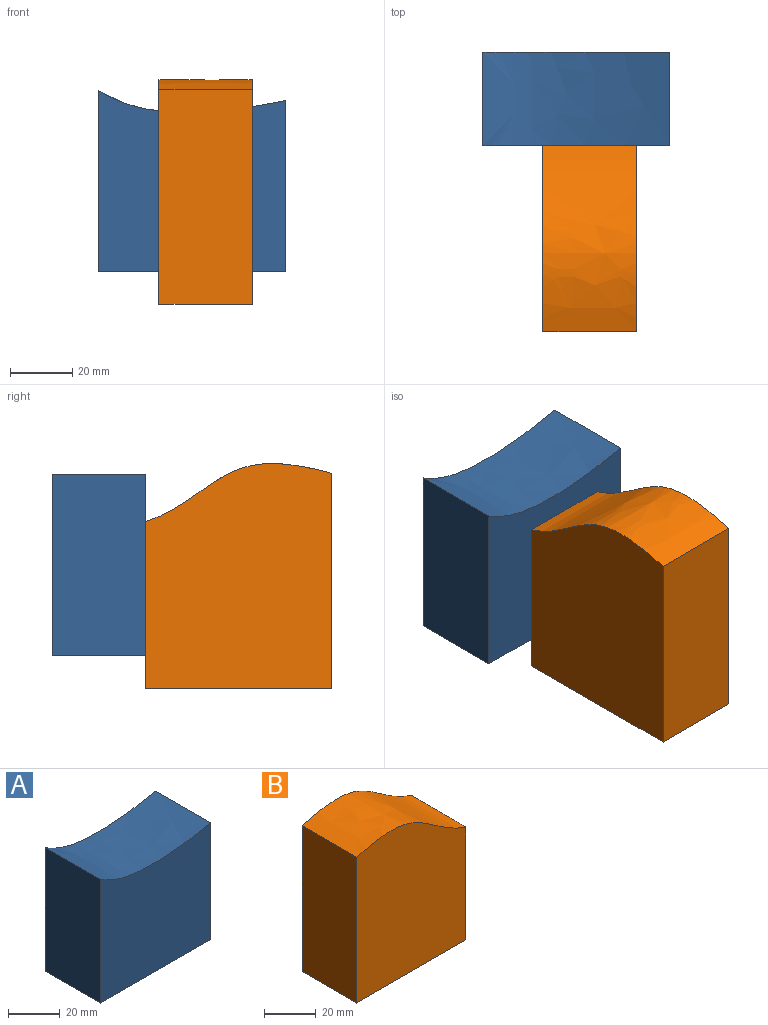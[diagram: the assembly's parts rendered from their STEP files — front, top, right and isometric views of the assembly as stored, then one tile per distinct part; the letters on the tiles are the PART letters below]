
ASSEMBLY  parts=2 mates=1
PART A: 6 faces, bbox 61.7x30x59.2 mm
  f0: extruded ~60x30mm, area 1847.2mm2, adj f2,f3,f4,f5
  f1: plane 60x30mm, normal (0,0,-1), area 1800mm2, adj f2,f3,f4,f5
  f2: plane 61.72x59.16mm, normal (0,1,0), area 3176.1mm2, adj f0,f1,f3,f5
  f3: plane 58.3x30mm, normal (-1,0,0), area 1749.1mm2, adj f0,f1,f2,f4
  f4: plane 61.72x59.16mm, normal (0,-1,0), area 3176.1mm2, adj f0,f1,f3,f5
  f5: plane 55.11x30mm, normal (1,0,0), area 1653.4mm2, adj f0,f1,f2,f4
PART B: 6 faces, bbox 61.8x30x73.3 mm
  f0: extruded ~60x30mm, area 1953mm2, adj f2,f3,f4,f5
  f1: plane 60x30mm, normal (0,0,-1), area 1800mm2, adj f2,f3,f4,f5
  f2: plane 73.31x61.83mm, normal (0,1,0), area 3999.4mm2, adj f0,f1,f3,f5
  f3: plane 69.28x30mm, normal (-1,0,0), area 2078.2mm2, adj f0,f1,f2,f4
  f4: plane 73.31x61.83mm, normal (0,-1,0), area 3999.4mm2, adj f0,f1,f3,f5
  f5: plane 53.69x30mm, normal (1,0,0), area 1610.7mm2, adj f0,f1,f2,f4
PLACE A t=(-41.58,-1.12,31.52)mm
PLACE B rot(axis=(0,0,1),90deg) t=(-2.21,-1.12,21)mm fixed
MATE planar B.f5 <-> A.f4  axis (0,1,0) through (-17.21,-1.12,32.94)mm
